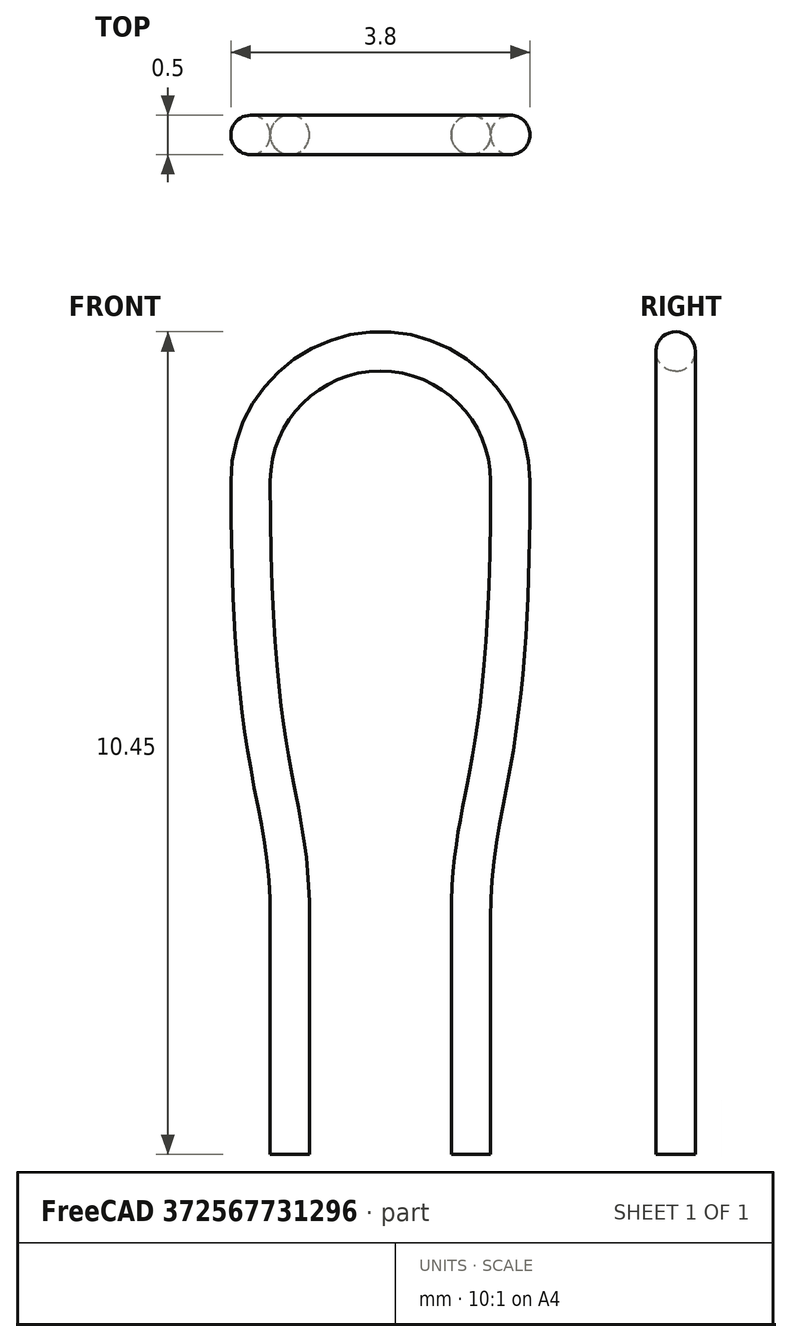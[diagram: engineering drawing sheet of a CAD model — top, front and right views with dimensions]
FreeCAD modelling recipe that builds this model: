
FCSTD DOCUMENT  (FreeCAD 0.17R12018 (Git))
Label: Test_Point_Loop_D3.80mm_Drill2.8mm
License: All rights reserved
LicenseURL: http://en.wikipedia.org/wiki/All_rights_reserved
objects: Sketcher::SketchObject×2, Spreadsheet::Sheet×1, PartDesign::AdditivePipe×1, PartDesign::Body×1, App::Part×1
note: 5 computed .brp shape members not serialized (recipe doc carries the construction recipe); baked Part::Feature solids carry a one-line shape summary decoded from their .brp

FEATURE [Spreadsheet::Sheet] Spreadsheet  label="dims"
  cells = A1="DWire"; B1(DWire)=0.5; A2="DLoop"; B2(DLoop)=3.7999999999999998; A3="Spacer"; B3(Spacer)=0; A4="DSpacer"; B4(DSpacer)=3; A5="Lall"; B5(Lall)=10.199999999999999; A6="Ddrill"; B6(Ddrill)=2.7999999999999998; A7="Lbottom"; B7(Lbottom)=3
FEATURE [Sketcher::SketchObject] Sketch001
  MapMode = 5
  Placement = pos=(0,0,0) rot=(1,0,0;1.5708rad)
  expr: Constraints[63] = (dims.DLoop - dims.DWire) / 2
  expr: Constraints[28] = dims.Lall - (dims.DLoop - dims.DWire) / 2
  expr: Constraints[27] = (dims.DLoop - dims.DWire) / 2
  expr: Constraints[30] = dims.Lbottom
  expr: Constraints[32] = dims.Spacer
  expr: Constraints[33] = dims.Ddrill - dims.DWire
  expr: Constraints[34] = (dims.Ddrill - dims.DWire) / 2
  sketch-geometry (25):
    g0: LineSegment StartX=-1.15 StartY=-3 StartZ=0 EndX=-1.15 EndY=0 EndZ=0
    g1: LineSegment StartX=1.14999 StartY=0 StartZ=0 EndX=1.14999 EndY=-3 EndZ=0
    g2: ArcOfCircle CenterX=0 CenterY=5.55 CenterZ=0 NormalX=0 NormalY=0 NormalZ=1 Radius=1.65 StartAngle=0 EndAngle=3.14159
    g3: LineSegment [constr] StartX=-1.65 StartY=5.55 StartZ=0 EndX=1.65 EndY=5.55 EndZ=0
    g4: LineSegment [constr] StartX=-1.65 StartY=0 StartZ=0 EndX=1.65 EndY=0 EndZ=0
    g5: LineSegment [constr] StartX=1.65 StartY=5.55 StartZ=0 EndX=1.65 EndY=0 EndZ=0
    g6: LineSegment [constr] StartX=-1.65 StartY=0 StartZ=0 EndX=-1.65 EndY=5.55 EndZ=0
    g7: LineSegment [constr] StartX=-1.15 StartY=0 StartZ=0 EndX=-1.15 EndY=1.65 EndZ=0
    g8: LineSegment [constr] StartX=1.14999 StartY=0 StartZ=0 EndX=1.14999 EndY=1.65 EndZ=0
    g9: LineSegment [constr] StartX=-1.65 StartY=1.65 StartZ=0 EndX=1.65 EndY=1.65 EndZ=0
    g10: LineSegment [constr] StartX=1.14999 StartY=1.65 StartZ=0 EndX=1.14999 EndY=5.55 EndZ=0
    g11-g14: Circle [constr] x4 (B-spline internal-alignment scaffolding for g15; pole/knot coordinates omitted)
    g15: BSplineCurve PolesCount=4 KnotsCount=2 Degree=3 IsPeriodic=0
    g16: GeomPoint [constr] X=-1.15 Y=0 Z=0
    g17: GeomPoint [constr] X=-1.65 Y=5.55 Z=0
    g18-g21: Circle [constr] x4 (B-spline internal-alignment scaffolding for g22; pole/knot coordinates omitted)
    g22: BSplineCurve PolesCount=4 KnotsCount=2 Degree=3 IsPeriodic=0
    g23: GeomPoint [constr] X=1.14999 Y=0 Z=0
    g24: GeomPoint [constr] X=1.65 Y=5.55 Z=0
  constraints (58):
    c: Vertical(g0)
    c: Vertical(g1)
    c: Coincident(g3,g2)
    c: Horizontal(g3)
    c: PointOnObject(g2,g3)
    c: Coincident(g3,g2)
    c: PointOnObject(g2,g-2)
    c: Horizontal(g4)
    c: Coincident(g5,g2)
    c: Coincident(g5,g4)
    c: Coincident(g6,g4)
    c: Coincident(g6,g2)
    c: PointOnObject(g0,g4)
    c: PointOnObject(g1,g4)
    c: Vertical(g6)
    c: Vertical(g5)
    c: Coincident(g7,g0)
    c: Vertical(g7)
    c: Coincident(g8,g1)
    c: Vertical(g8)
    c: PointOnObject(g9,g6)
    c: PointOnObject(g9,g5)
    c: Horizontal(g9)
    c: PointOnObject(g7,g9)
    c: PointOnObject(g8,g9)
    c: PointOnObject(g10,g3)
    c: Vertical(g10)
    c: Radius(g2) = 1.65
    c: DistanceY(g1,g2) = 8.55
    c: DistanceY(g1,g0) = 0
    c: DistanceY(g0,g-1) = 3
    c: Coincident(g10,g8)
    c: DistanceY(g-1,g0) = 0
    c: DistanceX(g0,g1) = 2.3
    c: DistanceX(g0,g-1) = 1.15
    c: Coincident(g11,g0)
    c: Radius(g11) = 0
    c: Equal(g11,g12)
    c: Coincident(g12,g7)
    c: Equal(g11,g13)
    c: Coincident(g13,g9)
    c: Equal(g11,g14)
    c: Coincident(g14,g2)
    c: InternalAlignment(g11-g14 -> g15) x4
    c: InternalAlignment(g16,g15)
    c: InternalAlignment(g17,g15)
    c: Coincident(g18,g1)
    c: Radius(g18) = 0
    c: Equal(g18,g19)
    c: Coincident(g19,g8)
    c: Equal(g18,g20)
    c: Coincident(g20,g9)
    c: Equal(g18,g21)
    c: Coincident(g21,g2)
    c: InternalAlignment(g18-g21 -> g22) x4
    c: InternalAlignment(g23,g22)
    c: InternalAlignment(g24,g22)
    c: DistanceY(g4,g9) = 1.65
FEATURE [Sketcher::SketchObject] Sketch
  MapMode = 5
  Placement = pos=(0,0,-3) rot=(0,0,1;0rad)
  expr: Constraints[2] = (dims.Ddrill - dims.DWire) / 2
  expr: Constraints[1] = dims.DWire / 2
  sketch-geometry (1):
    g0: Circle CenterX=-1.15 CenterY=0 CenterZ=0 NormalX=0 NormalY=0 NormalZ=1 Radius=0.25
  constraints (3):
    c: PointOnObject(g0,g-1)
    c: Radius(g0) = 0.25
    c: DistanceX(g0,g-1) = 1.15
FEATURE [PartDesign::AdditivePipe] AdditivePipe
  AuxilleryCurvelinear = true
  AuxillerySpineTangent = false
  Binormal = (0,0,0)
  Mode = 0
  Placement = pos=(0,0,-3) rot=(0,0,1;0rad)
  Profile = -> Sketch
  Spine = -> Sketch001 [Edge1,Edge2,Edge3,Edge4,Edge5]
  SpineTangent = false
  Transformation = 0
  Transition = 0
FEATURE [PartDesign::Body] Body  label="Test_Point_Loop_D3.80mm_Drill2.8mm"
  Group = -> [Sketch,Sketch001,AdditivePipe]
  Origin = -> Origin002
  Tip = -> AdditivePipe
FEATURE [App::Part] Part  label="group"
  Group = -> [Body]
  License = CC BY 3.0
  LicenseURL = http://creativecommons.org/licenses/by/3.0/
  Origin = -> Origin
